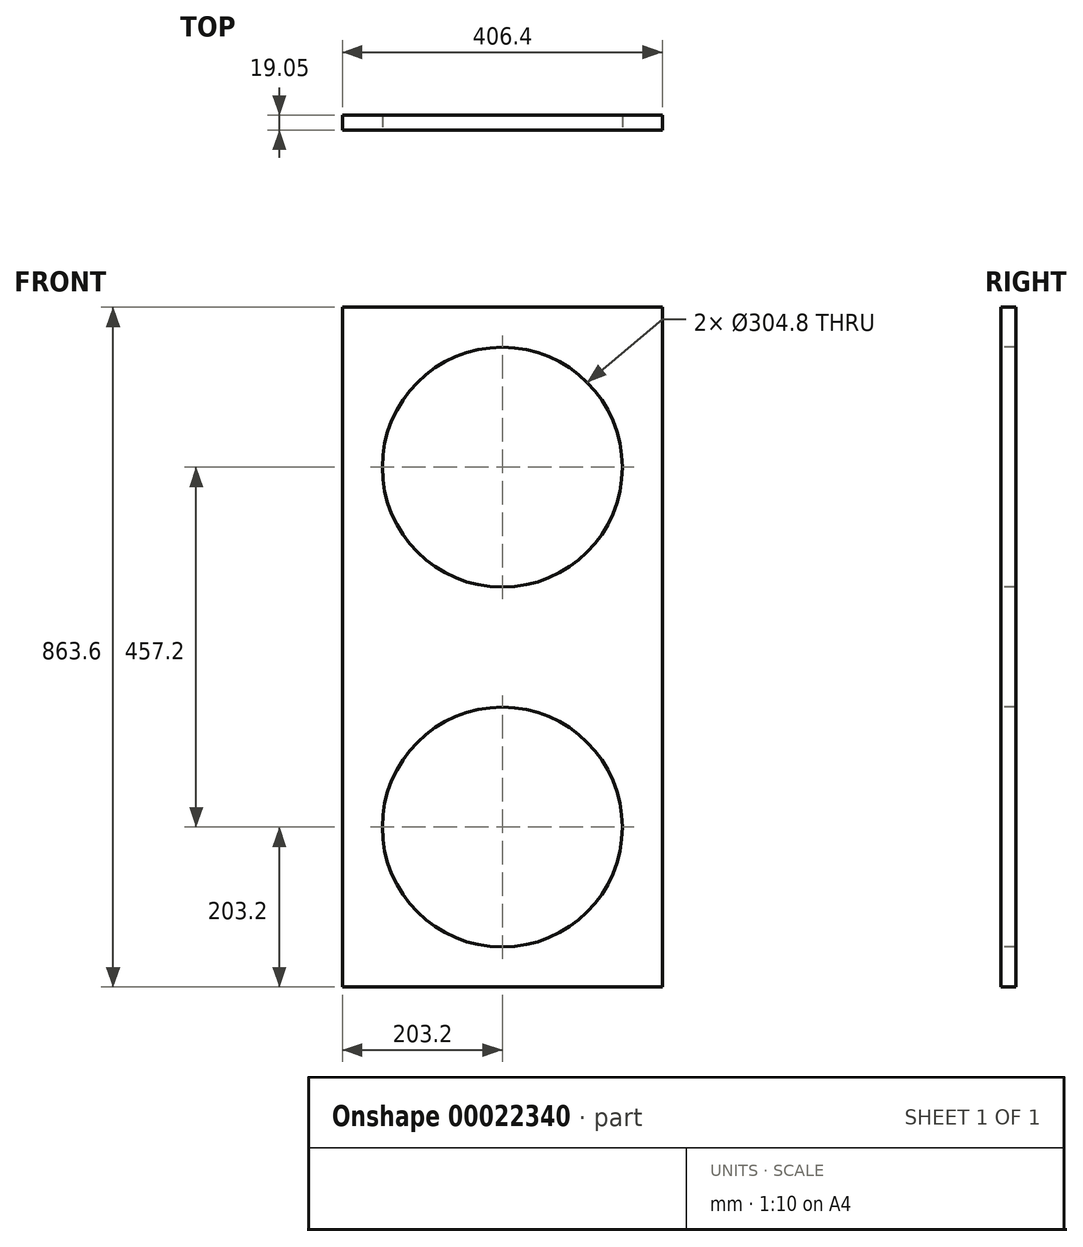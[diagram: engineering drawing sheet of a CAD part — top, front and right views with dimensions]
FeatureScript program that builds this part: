
annotation { "Feature Type Name" : "Feature", "Feature Type Description" : "" }
export const myFeature = defineFeature(function(context is Context, id is Id, definition is map)
    precondition{}
    {
        {
            var Q0;
            Q0=qCreatedBy(makeId("Front.planeOp"),FACE);
            var sketch = newSketch(context, id + "F0", { "sketchPlane" : qUnion([Q0])});
            skLineSegment(sketch, "E0.rect.bottom", {"start": v(228.6, 431.8) * mm, "end": v(-228.6, 431.8) * mm});
            skLineSegment(sketch, "E0.rect.top", {"start": v(228.6, -431.8) * mm, "end": v(-228.6, -431.8) * mm});
            skLineSegment(sketch, "E0.rect.left", {"start": v(228.6, 431.8) * mm, "end": v(228.6, -431.8) * mm});
            skLineSegment(sketch, "E0.rect.right", {"start": v(-228.6, 431.8) * mm, "end": v(-228.6, -431.8) * mm});
            skPoint(sketch, "E0.rect.middle", {"position": v(0, 0) * mm});
            skSolve(sketch);
        }
        {
            var Q0;
            Q0=makeQuery(id+"F0.imprint","IMPRINT",FACE,{"disambiguationData":[TD([[makeQuery(id+"F0.imprint","IMPRINT",EDGE,{"derivedFrom":sQuery(id+"F0.wireOp",EDGE,"E0.rect.bottom")}),1.0]])]});
            extrude(context, id + "F1", {"entities" : qUnion([Q0]), "depth" : 19.05 * mm});
        }
        {
            var Q0;
            Q0=makeQuery(id+"F1.opExtrude","CAP_FACE",FACE,{"disambiguationData":[OSD([sQuery(id+"F0.wireOp",EDGE,"E0.rect.bottom"),sQuery(id+"F0.wireOp",EDGE,"E0.rect.top"),sQuery(id+"F0.wireOp",EDGE,"E0.rect.left"),sQuery(id+"F0.wireOp",EDGE,"E0.rect.right")])],"isStart":false});
            var sketch = newSketch(context, id + "F2", { "sketchPlane" : qUnion([Q0])});
            skCircle(sketch, "E1", {"center": v(-25.4, 228.6) * mm, "radius": 152.4 * mm});
            skCircle(sketch, "E2", {"center": v(-25.4, -228.6) * mm, "radius": 152.4 * mm});
            skLineSegment(sketch, "E3.bottom", {"start": v(228.6, 431.8) * mm, "end": v(177.8, 431.8) * mm});
            skLineSegment(sketch, "E3.top", {"start": v(228.6, -431.8) * mm, "end": v(177.8, -431.8) * mm});
            skLineSegment(sketch, "E3.left", {"start": v(228.6, 431.8) * mm, "end": v(228.6, -431.8) * mm});
            skLineSegment(sketch, "E3.right", {"start": v(177.8, 431.8) * mm, "end": v(177.8, -431.8) * mm});
            skSolve(sketch);
        }
        {
            var Q0;
            Q0=makeQuery(id+"F2.imprint","IMPRINT",FACE,{"disambiguationData":[TD([[makeQuery(id+"F2.imprint","IMPRINT",EDGE,{"derivedFrom":sQuery(id+"F2.wireOp",EDGE,"E1")}),1.0]])]});
            var Q1;
            Q1=makeQuery(id+"F2.imprint","IMPRINT",FACE,{"disambiguationData":[TD([[makeQuery(id+"F2.imprint","IMPRINT",EDGE,{"derivedFrom":sQuery(id+"F2.wireOp",EDGE,"E2")}),1.0]])]});
            var Q2;
            Q2=makeQuery(id+"F2.imprint","IMPRINT",FACE,{"disambiguationData":[TD([[makeQuery(id+"F2.imprint","IMPRINT",EDGE,{"derivedFrom":sQuery(id+"F2.wireOp",EDGE,"E3.bottom")}),1.0]])]});
            extrude(context, id + "F3", {"entities" : qUnion([Q0, Q1, Q2]), "operationType" : NewBodyOperationType.REMOVE, "oppositeDirection" : true, "depth" : 25.4 * mm});
        }
    });
